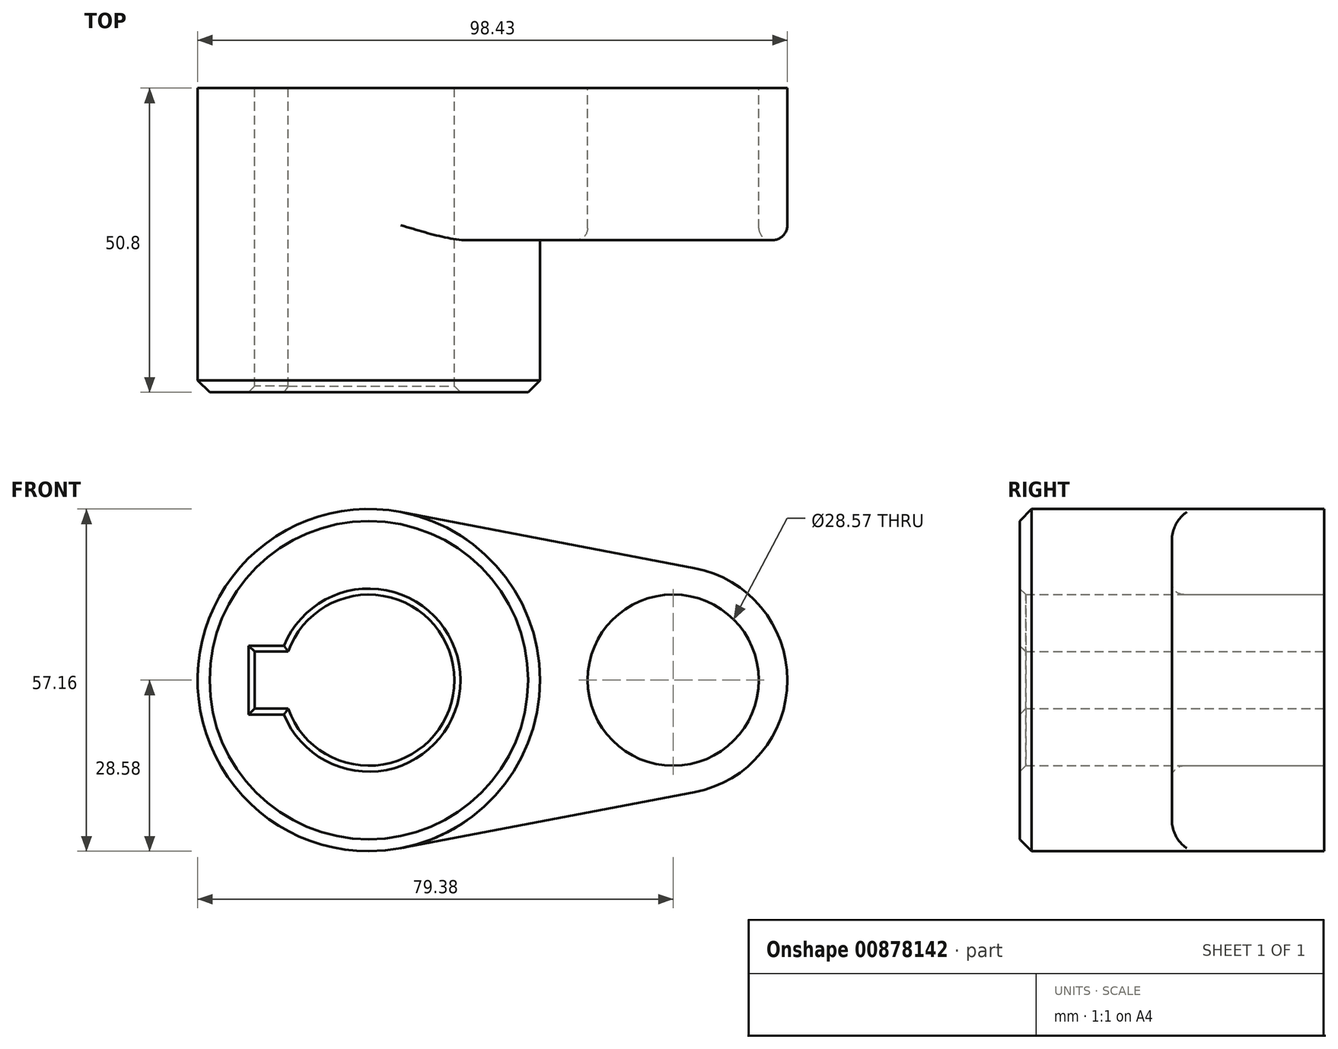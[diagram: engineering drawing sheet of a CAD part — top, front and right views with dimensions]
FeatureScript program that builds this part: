
annotation { "Feature Type Name" : "Feature", "Feature Type Description" : "" }
export const myFeature = defineFeature(function(context is Context, id is Id, definition is map)
    precondition{}
    {
        {
            var Q0;
            Q0=qCreatedBy(makeId("Front.planeOp"),FACE);
            var sketch = newSketch(context, id + "F0", { "sketchPlane" : qUnion([Q0])});
            skCircle(sketch, "E0", {"center": v(0, 0) * mm, "radius": 28.58 * mm});
            skCircle(sketch, "E1", {"center": v(50.8, 0) * mm, "radius": 19.05 * mm});
            skLineSegment(sketch, "E2", {"start": v(5.36, 28.07) * mm, "end": v(54.37, 18.71) * mm});
            skLineSegment(sketch, "E3", {"start": v(5.36, -28.07) * mm, "end": v(54.37, -18.71) * mm});
            skCircle(sketch, "E4", {"center": v(0, 0) * mm, "radius": 14.29 * mm});
            skCircle(sketch, "E5", {"center": v(50.8, 0) * mm, "radius": 14.29 * mm});
            skLineSegment(sketch, "E6.bottom", {"start": v(-19.05, 4.76) * mm, "end": v(19.05, 4.76) * mm});
            skLineSegment(sketch, "E6.top", {"start": v(-19.05, -4.76) * mm, "end": v(19.05, -4.76) * mm});
            skLineSegment(sketch, "E6.left", {"start": v(-19.05, 4.76) * mm, "end": v(-19.05, -4.76) * mm});
            skLineSegment(sketch, "E6.right", {"start": v(19.05, 4.76) * mm, "end": v(19.05, -4.76) * mm});
            skFitSpline(sketch, "E7", {"points": [v(39.13, -21.62) * mm, v(65.37, -36.96) * mm, v(79.8, -20.44) * mm, v(82.3, 24.83) * mm, v(54.37, 18.71) * mm], "startDerivative": vector(115.07, -94.4) * mm, "endDerivative": vector(-142.63, -70.88) * mm});
            skSolve(sketch);
        }
        {
            var Q0;
            Q0=makeQuery(id+"F0.imprint","IMPRINT",FACE,{"disambiguationData":[TD([[makeQuery(id+"F0.imprint","IMPRINT",EDGE,{"derivedFrom":sQuery(id+"F0.wireOp",EDGE,"E5")}),-1.0]])]});
            var Q1;
            {var subQ0=sQuery(id+"F0.wireOp",EDGE,"E2");Q1=makeQuery(id+"F0.imprint","IMPRINT",FACE,{"disambiguationData":[TD([[makeQuery(id+"F0.imprint","IMPRINT",EDGE,{"derivedFrom":subQ0}),-1.0]])]});}
            var Q2;
            {var subQ7=sQuery(id+"F0.wireOp",EDGE,"E6.left");Q2=makeQuery(id+"F0.imprint","IMPRINT",FACE,{"disambiguationData":[TD([[makeQuery(id+"F0.imprint","IMPRINT",EDGE,{"derivedFrom":subQ7}),-1.0]])]});}
            var Q3;
            {var subQ5=sQuery(id+"F0.wireOp",EDGE,"E6.right");Q3=makeQuery(id+"F0.imprint","IMPRINT",FACE,{"disambiguationData":[TD([[makeQuery(id+"F0.imprint","IMPRINT",EDGE,{"derivedFrom":subQ5}),-1.0]])]});}
            extrude(context, id + "F1", {"entities" : qUnion([Q0, Q1, Q2, Q3]), "depth" : 25.4 * mm, "offsetDistance" : 25.4 * mm});
        }
        {
            var Q0;
            {var subQ7=sQuery(id+"F0.wireOp",EDGE,"E6.left");Q0=makeQuery(id+"F0.imprint","IMPRINT",FACE,{"disambiguationData":[TD([[makeQuery(id+"F0.imprint","IMPRINT",EDGE,{"derivedFrom":subQ7}),-1.0]])]});}
            var Q1;
            {var subQ5=sQuery(id+"F0.wireOp",EDGE,"E6.right");Q1=makeQuery(id+"F0.imprint","IMPRINT",FACE,{"disambiguationData":[TD([[makeQuery(id+"F0.imprint","IMPRINT",EDGE,{"derivedFrom":subQ5}),-1.0]])]});}
            extrude(context, id + "F2", {"entities" : qUnion([Q0, Q1]), "operationType" : NewBodyOperationType.ADD, "depth" : 50.8 * mm, "offsetDistance" : 25.4 * mm});
        }
        {
            var Q0;
            Q0=makeQuery(id+"F1.opExtrude","CAP_EDGE",EDGE,{"disambiguationData":[OSD([sQuery(id+"F0.wireOp",EDGE,"E3")])],"isStart":false});
            fillet(context, id + "F3", {"entities" : qUnion([Q0]), "radius" : 2.5 * mm, "tangentPropagation" : true, "allowEdgeOverflow" : false});
        }
        {
            var Q0;
            Q0=makeQuery(id+"F2.opExtrude","CAP_EDGE",EDGE,{"disambiguationData":[OSD([sQuery(id+"F0.wireOp",EDGE,"E0")])],"isStart":false});
            chamfer(context, id + "F4", {"entities" : qUnion([Q0]), "width" : 2 * mm, "tangentPropagation" : true});
        }
        {
            var Q0;
            Q0=makeQuery(id+"F2.opExtrude","CAP_EDGE",EDGE,{"disambiguationData":[OSD([sQuery(id+"F0.wireOp",EDGE,"E4")])],"isStart":false});
            var Q1;
            Q1=makeQuery(id+"F2.opExtrude","CAP_EDGE",EDGE,{"disambiguationData":[OSD([sQuery(id+"F0.wireOp",EDGE,"E6.left")])],"isStart":false});
            var Q2;
            Q2=makeQuery(id+"F2.opExtrude","CAP_EDGE",EDGE,{"disambiguationData":[OSD([sQuery(id+"F0.wireOp",EDGE,"E6.top")])],"isStart":false});
            var Q3;
            Q3=makeQuery(id+"F2.opExtrude","CAP_EDGE",EDGE,{"disambiguationData":[OSD([sQuery(id+"F0.wireOp",EDGE,"E6.bottom")])],"isStart":false});
            chamfer(context, id + "F5", {"entities" : qUnion([Q0, Q1, Q2, Q3]), "width" : 1 * mm, "tangentPropagation" : true});
        }
        {
            var Q0;
            Q0=makeQuery(id+"F1.opExtrude","CAP_EDGE",EDGE,{"disambiguationData":[OSD([sQuery(id+"F0.wireOp",EDGE,"E5")])],"isStart":false});
            fillet(context, id + "F6", {"entities" : qUnion([Q0]), "radius" : 2 * mm, "tangentPropagation" : true, "allowEdgeOverflow" : false});
        }
    });
